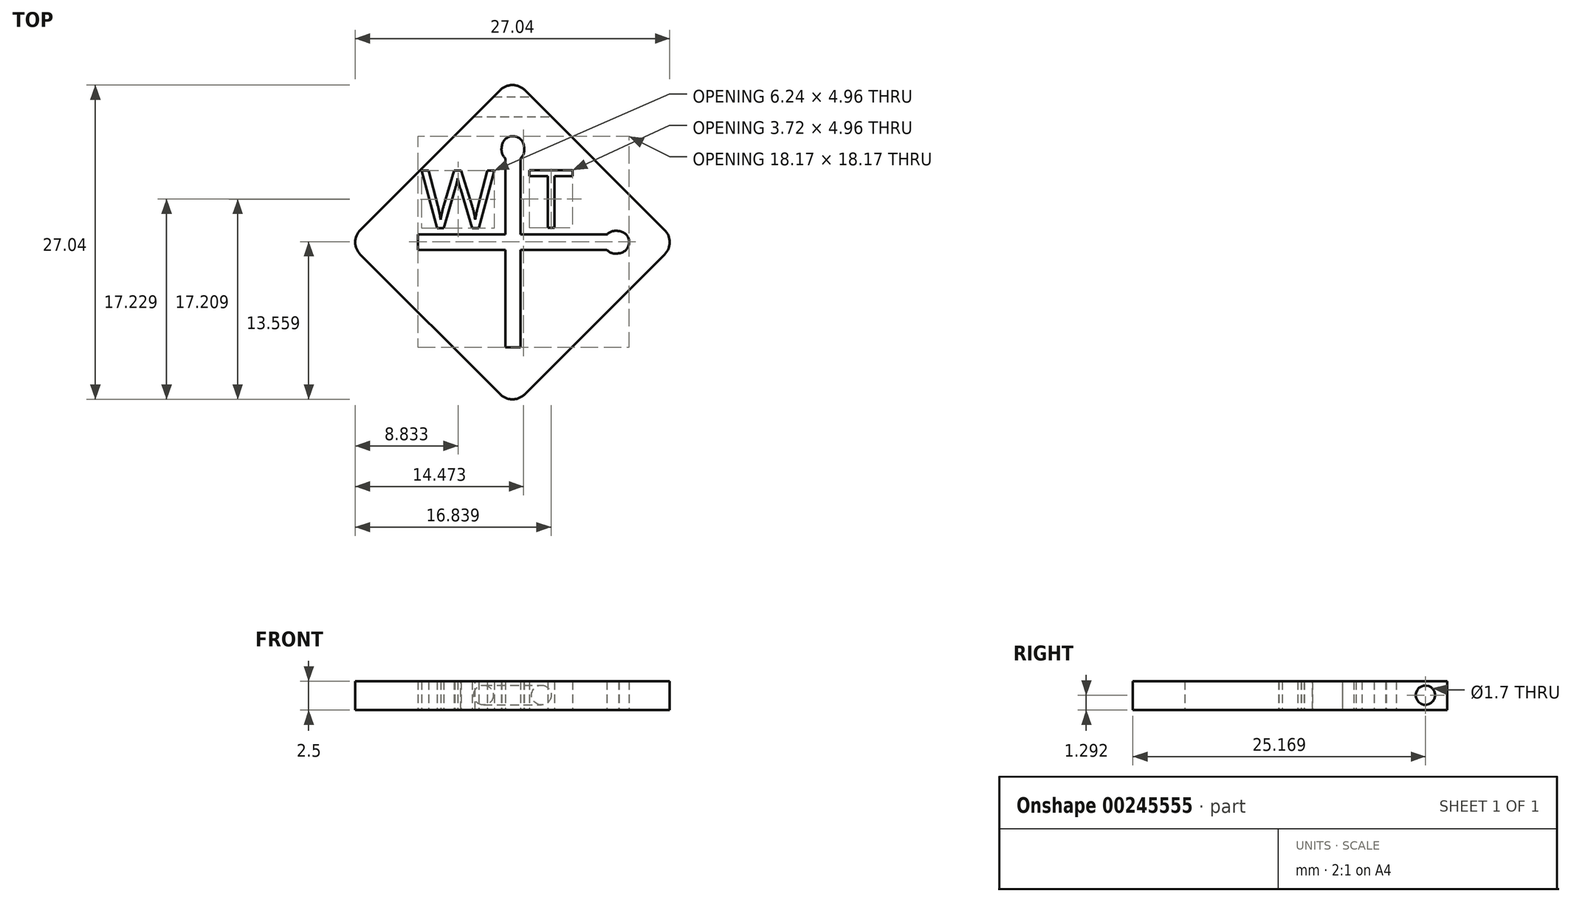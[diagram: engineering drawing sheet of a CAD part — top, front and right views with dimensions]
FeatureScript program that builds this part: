
annotation { "Feature Type Name" : "Feature", "Feature Type Description" : "" }
export const myFeature = defineFeature(function(context is Context, id is Id, definition is map)
    precondition{}
    {
        {
            var Q0;
            Q0=qCreatedBy(makeId("Top.planeOp"),FACE);
            var sketch = newSketch(context, id + "F0", { "sketchPlane" : qUnion([Q0])});
            skLineSegment(sketch, "E0", {"start": v(1.06, -1.06) * mm, "end": v(13.08, -13.08) * mm});
            skLineSegment(sketch, "E1", {"start": v(13.08, -15.2) * mm, "end": v(1.06, -27.22) * mm});
            skLineSegment(sketch, "E2", {"start": v(-1.06, -27.22) * mm, "end": v(-13.08, -15.2) * mm});
            skLineSegment(sketch, "E3", {"start": v(-13.08, -13.08) * mm, "end": v(-1.06, -1.06) * mm});
            skPoint(sketch, "E4.visualSharp", {"position": v(0, 0) * mm});
            skArc(sketch, "E4.filletArc", {"start": v(1.06, -1.06) * mm, "mid": v(0, -0.62) * mm, "end": v(-1.06, -1.06) * mm});
            skPoint(sketch, "E5.visualSharp", {"position": v(-14.14, -14.14) * mm});
            skArc(sketch, "E5.filletArc", {"start": v(-13.08, -13.08) * mm, "mid": v(-13.52, -14.14) * mm, "end": v(-13.08, -15.2) * mm});
            skPoint(sketch, "E6.visualSharp", {"position": v(14.14, -14.14) * mm});
            skArc(sketch, "E6.filletArc", {"start": v(13.08, -15.2) * mm, "mid": v(13.52, -14.14) * mm, "end": v(13.08, -13.08) * mm});
            skPoint(sketch, "E7.visualSharp", {"position": v(0, -28.28) * mm});
            skArc(sketch, "E7.filletArc", {"start": v(-1.06, -27.22) * mm, "mid": v(0, -27.66) * mm, "end": v(1.06, -27.22) * mm});
            skLineSegment(sketch, "E8", {"start": v(0, 0) * mm, "end": v(0, -31.86) * mm, "construction": true});
            skLineSegment(sketch, "E9", {"start": v(-14.14, -14.14) * mm, "end": v(14.14, -14.14) * mm, "construction": true});
            skLineSegment(sketch, "E10", {"start": v(-8.13, -13.48) * mm, "end": v(-8.13, -14.8) * mm});
            skLineSegment(sketch, "E11", {"start": v(-8.13, -14.8) * mm, "end": v(8.13, -14.8) * mm});
            skLineSegment(sketch, "E12", {"start": v(8.13, -13.48) * mm, "end": v(-8.13, -13.48) * mm});
            skLineSegment(sketch, "E13", {"start": v(-8.13, -13.48) * mm, "end": v(0, -13.48) * mm, "construction": true});
            skLineSegment(sketch, "E14", {"start": v(0, -13.48) * mm, "end": v(8.13, -13.48) * mm, "construction": true});
            skArc(sketch, "E15", {"start": v(9.18, -15.1) * mm, "mid": v(10.04, -14.12) * mm, "end": v(9.13, -13.2) * mm});
            skArc(sketch, "E16", {"start": v(9.13, -13.2) * mm, "mid": v(8.6, -13.2) * mm, "end": v(8.13, -13.48) * mm});
            skArc(sketch, "E17", {"start": v(8.13, -14.8) * mm, "mid": v(8.61, -15.1) * mm, "end": v(9.18, -15.1) * mm});
            skLineSegment(sketch, "E18", {"start": v(-0.62, -23.19) * mm, "end": v(0.7, -23.19) * mm});
            skLineSegment(sketch, "E19", {"start": v(0.7, -23.19) * mm, "end": v(0.7, -6.92) * mm});
            skLineSegment(sketch, "E20", {"start": v(-0.62, -6.92) * mm, "end": v(-0.62, -23.19) * mm});
            skLineSegment(sketch, "E21", {"start": v(-0.62, -23.19) * mm, "end": v(-0.62, -15.05) * mm, "construction": true});
            skLineSegment(sketch, "E22", {"start": v(-0.62, -15.05) * mm, "end": v(-0.62, -6.92) * mm, "construction": true});
            skArc(sketch, "E23", {"start": v(0.99, -5.88) * mm, "mid": v(0.02, -5.01) * mm, "end": v(-0.91, -5.92) * mm});
            skArc(sketch, "E24", {"start": v(-0.91, -5.92) * mm, "mid": v(-0.9, -6.46) * mm, "end": v(-0.62, -6.92) * mm});
            skArc(sketch, "E25", {"start": v(0.7, -6.92) * mm, "mid": v(1, -6.44) * mm, "end": v(0.99, -5.88) * mm});
            skText(sketch, "E26", { "text": "W", "fontName": "OpenSans-Regular.ttf"});
            skText(sketch, "E27", { "text": "T", "fontName": "OpenSans-Regular.ttf"});
            const initialGuessF0  = {"E26": [-0.0079, -0.01293, 1, 0, 0.005], "E27": [0.0014, -0.01291, 1, 0, 0.005]};
            skSetInitialGuess(sketch, initialGuessF0);
            skSolve(sketch);
        }
        {
            var Q0;
            Q0=makeQuery(id+"F0.imprint","IMPRINT",FACE,{"disambiguationData":[TD([[makeQuery(id+"F0.imprint","IMPRINT",EDGE,{"derivedFrom":sQuery(id+"F0.wireOp",EDGE,"E0")}),-1.0]])]});
            extrude(context, id + "F1", {"entities" : qUnion([Q0]), "depth" : 2.5 * mm});
        }
        {
            var Q0;
            Q0=qCreatedBy(makeId("Right.planeOp"),FACE);
            var sketch = newSketch(context, id + "F2", { "sketchPlane" : qUnion([Q0])});
            skCircle(sketch, "E28", {"center": v(-2.5, 1.3) * mm, "radius": 0.85 * mm});
            skSolve(sketch);
        }
        {
            var Q0;
            Q0=qSketchRegion(id+"F2",true);
            extrude(context, id + "F3", {"entities" : qUnion([Q0]), "operationType" : NewBodyOperationType.REMOVE, "endBound" : BoundingType.SYMMETRIC, "oppositeDirection" : true, "depth" : 25 * mm});
        }
    });
